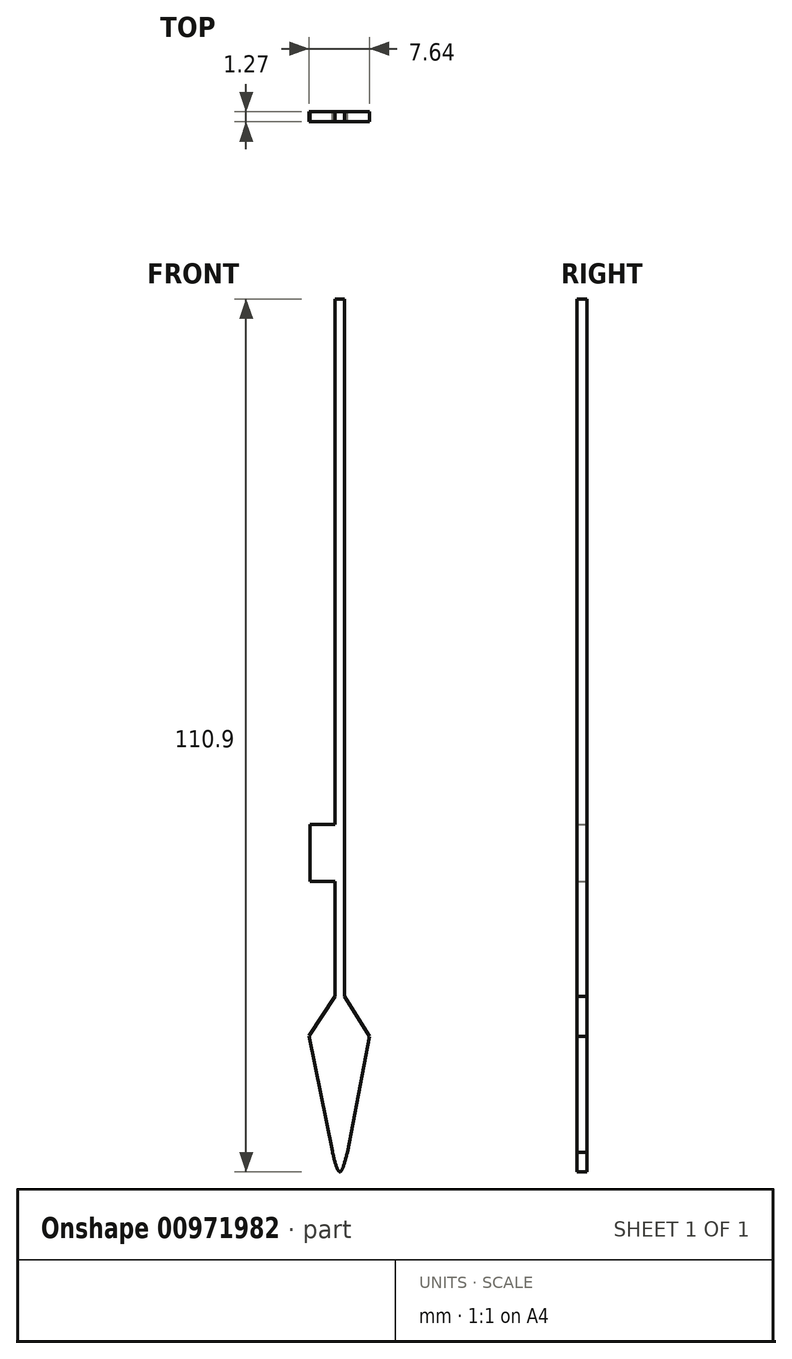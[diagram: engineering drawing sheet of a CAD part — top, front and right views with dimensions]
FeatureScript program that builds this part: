
annotation { "Feature Type Name" : "Feature", "Feature Type Description" : "" }
export const myFeature = defineFeature(function(context is Context, id is Id, definition is map)
    precondition{}
    {
        {
            var Q0;
            Q0=qCreatedBy(makeId("Front.planeOp"),FACE);
            var sketch = newSketch(context, id + "F0", { "sketchPlane" : qUnion([Q0])});
            skLineSegment(sketch, "E0.bottom", {"start": v(-1.3, 3.4) * mm, "end": v(-0.07, 3.4) * mm});
            skLineSegment(sketch, "E0.top", {"start": v(-1.3, -85.17) * mm, "end": v(-0.07, -85.17) * mm});
            skLineSegment(sketch, "E0.left", {"start": v(-1.3, 3.4) * mm, "end": v(-1.3, -85.17) * mm});
            skLineSegment(sketch, "E0.right", {"start": v(-0.07, 3.4) * mm, "end": v(-0.07, -85.17) * mm});
            skLineSegment(sketch, "E1", {"start": v(-1.3, -85.17) * mm, "end": v(-4.57, -90.2) * mm});
            skLineSegment(sketch, "E2", {"start": v(-0.07, -85.17) * mm, "end": v(3.07, -90.29) * mm});
            skLineSegment(sketch, "E3", {"start": v(-4.57, -90.2) * mm, "end": v(-1.63, -104.91) * mm});
            skLineSegment(sketch, "E4", {"start": v(-0.68, -85.17) * mm, "end": v(-0.68, -107.5) * mm});
            skLineSegment(sketch, "E5", {"start": v(3.07, -90.29) * mm, "end": v(0.28, -105.04) * mm});
            skLineSegment(sketch, "E6", {"start": v(-1.63, -104.91) * mm, "end": v(-0.68, -104.91) * mm});
            skLineSegment(sketch, "E7", {"start": v(0.28, -105.04) * mm, "end": v(-0.68, -104.91) * mm});
            skFitSpline(sketch, "E8", {"points": [v(-1.63, -104.91) * mm, v(-0.68, -107.5) * mm, v(0.28, -105.04) * mm], "startDerivative": vector(1.88, -7.65) * mm, "endDerivative": vector(1.95, 7.45) * mm});
            skLineSegment(sketch, "E9", {"start": v(-1.3, -85.17) * mm, "end": v(-1.3, -70.58) * mm});
            skLineSegment(sketch, "E10.bottom", {"start": v(-1.3, -70.58) * mm, "end": v(-4.5, -70.58) * mm});
            skLineSegment(sketch, "E10.top", {"start": v(-1.3, -63.33) * mm, "end": v(-4.5, -63.33) * mm});
            skLineSegment(sketch, "E10.left", {"start": v(-1.3, -70.58) * mm, "end": v(-1.3, -63.33) * mm});
            skLineSegment(sketch, "E10.right", {"start": v(-4.5, -70.58) * mm, "end": v(-4.5, -63.33) * mm});
            skSolve(sketch);
        }
        {
            var Q0;
            Q0=makeQuery(id+"F0.imprint","IMPRINT",FACE,{"disambiguationData":[TD([[makeQuery(id+"F0.imprint","IMPRINT",EDGE,{"derivedFrom":sQuery(id+"F0.wireOp",EDGE,"E0.bottom")}),-1.0]])]});
            var Q1;
            Q1=makeQuery(id+"F0.imprint","IMPRINT",FACE,{"disambiguationData":[TD([[makeQuery(id+"F0.imprint","IMPRINT",EDGE,{"derivedFrom":sQuery(id+"F0.wireOp",EDGE,"E10.bottom")}),-1.0]])]});
            var Q2;
            {var subQ4=sQuery(id+"F0.wireOp",EDGE,"E1");Q2=makeQuery(id+"F0.imprint","IMPRINT",FACE,{"disambiguationData":[TD([[makeQuery(id+"F0.imprint","IMPRINT",EDGE,{"derivedFrom":subQ4}),1.0]])]});}
            var Q3;
            {var subQ4=sQuery(id+"F0.wireOp",EDGE,"E2");Q3=makeQuery(id+"F0.imprint","IMPRINT",FACE,{"disambiguationData":[TD([[makeQuery(id+"F0.imprint","IMPRINT",EDGE,{"derivedFrom":subQ4}),-1.0]])]});}
            var Q4;
            {var subQ3=sQuery(id+"F0.wireOp",EDGE,"E7");Q4=makeQuery(id+"F0.imprint","IMPRINT",FACE,{"disambiguationData":[TD([[makeQuery(id+"F0.imprint","IMPRINT",EDGE,{"derivedFrom":subQ3}),1.0]])]});}
            var Q5;
            {var subQ3=sQuery(id+"F0.wireOp",EDGE,"E6");Q5=makeQuery(id+"F0.imprint","IMPRINT",FACE,{"disambiguationData":[TD([[makeQuery(id+"F0.imprint","IMPRINT",EDGE,{"derivedFrom":subQ3}),-1.0]])]});}
            extrude(context, id + "F1", {"entities" : qUnion([Q0, Q1, Q2, Q3, Q4, Q5]), "depth" : 1.27 * mm, "offsetDistance" : 25.4 * mm});
        }
    });
